# Revit family: Legrand coffret XL3 HP 630
name_source: partatom
category: Modèles génériques
units: mm (PartAtom-declared; Revit-internal decimal feet)

## family parameters
Conserver l'orientation des annotations = Non
Cote de connecteur circulaire = Utiliser le diamètre
Couper avec des vides une fois chargée = Non
Hôte = Mur
Numéro OmniClass = 23.80.30.11.17
Partagée = Non
Peut héberger une armature = Non
Repère de localisation dans la pièce = Non
Titre OmniClass = Distribution Boards and Control Panels
Toujours verticalement = Oui
Type d'élément = Normal

## types (2) — shared parameters
Classification d'isolation électrique = classe 1
Conditions Générale d'Utilisation = https://assets.legrand.com
Elévation par défaut = 1000 mm  [stored 3.28084 ft]
Fabricant = legrand
Hauteur du rack de 150 mm = 150 mm  [stored 0.492126 ft]
Hauteur du rack de 200 mm = 200 mm  [stored 0.656168 ft]
Indice de court-circuit = 50000 A
RAL = 7035
URL = https://www.legrand.fr

## per-type parameters (varying)
| type | IP 55 | Profondeur | Profondeur de rack | Profondeur zone installation | Référence de IP55 |
| Legrand coffret métal XL3 HP 630 | Non | 230 mm  [stored 0.754593 ft] | 230 mm  [stored 0.754593 ft] | 730 mm  [stored 2.39501 ft] | Non |
| Legrand coffret métal XL3 HP 630 IP55 | Oui | 252 mm  [stored 0.826772 ft] | 252 mm  [stored 0.826772 ft] | 752 mm  [stored 2.46719 ft] | Oui |

note: [stored X ft] marks values corroborated as IEEE doubles in the binary element streams (Revit-internal decimal feet)
